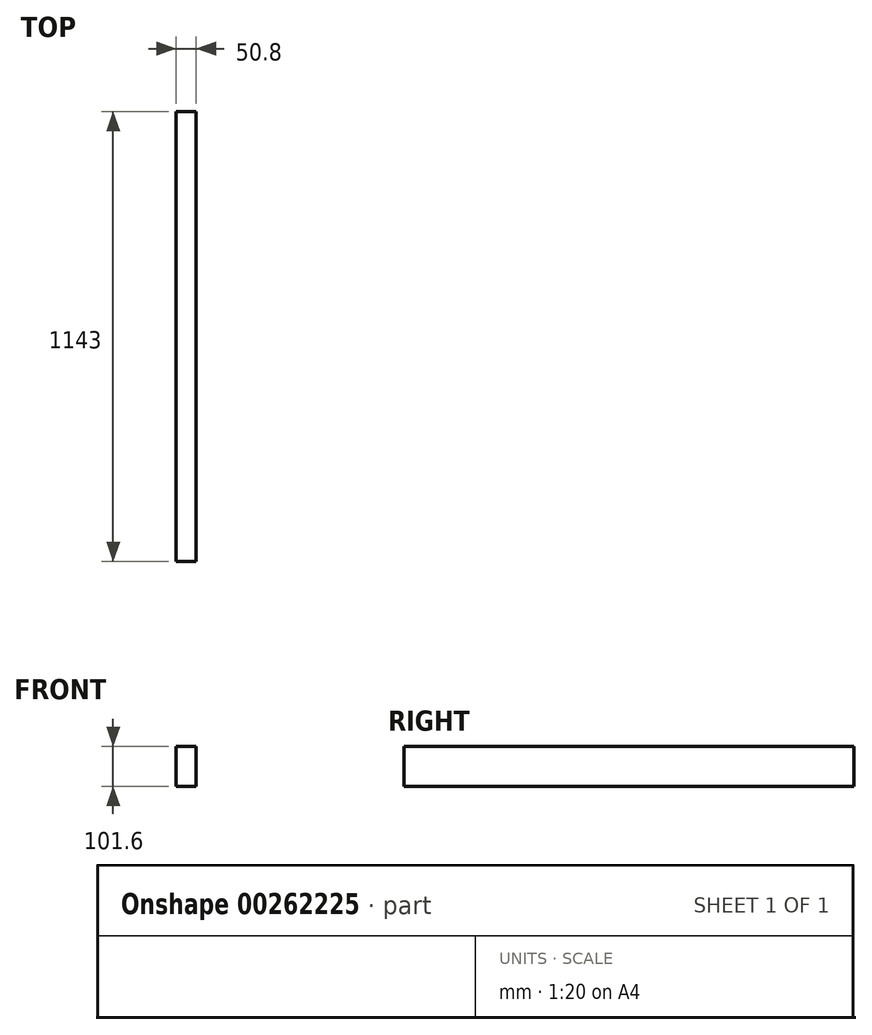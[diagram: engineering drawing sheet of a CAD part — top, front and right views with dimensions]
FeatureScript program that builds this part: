
annotation { "Feature Type Name" : "Feature", "Feature Type Description" : "" }
export const myFeature = defineFeature(function(context is Context, id is Id, definition is map)
    precondition{}
    {
        {
            var Q0;
            Q0=qCreatedBy(makeId("Front.planeOp"),FACE);
            var sketch = newSketch(context, id + "F0", { "sketchPlane" : qUnion([Q0])});
            skLineSegment(sketch, "E0.bottom", {"start": v(25.4, -50.8) * mm, "end": v(-25.4, -50.8) * mm});
            skLineSegment(sketch, "E0.top", {"start": v(25.4, 50.8) * mm, "end": v(-25.4, 50.8) * mm});
            skLineSegment(sketch, "E0.left", {"start": v(25.4, -50.8) * mm, "end": v(25.4, 50.8) * mm});
            skLineSegment(sketch, "E0.right", {"start": v(-25.4, -50.8) * mm, "end": v(-25.4, 50.8) * mm});
            skPoint(sketch, "E0.middle", {"position": v(0, 0) * mm});
            skSolve(sketch);
        }
        {
            var Q0;
            Q0=makeQuery(id+"F0.imprint","IMPRINT",FACE,{"disambiguationData":[TD([[makeQuery(id+"F0.imprint","IMPRINT",EDGE,{"derivedFrom":sQuery(id+"F0.wireOp",EDGE,"E0.bottom")}),-1.0]])]});
            extrude(context, id + "F1", {"entities" : qUnion([Q0]), "depth" : 1143 * mm});
        }
    });
